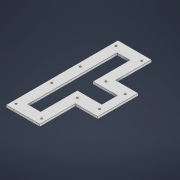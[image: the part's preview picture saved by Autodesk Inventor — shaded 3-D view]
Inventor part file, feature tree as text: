
AUTODESK INVENTOR PART (.ipt)
format: ipt  version: 2021 (Build 250183000, 183)  size: 371,712 bytes
history: native  units: mm
features: extrude x5, sketch x4, projected_geometry x1
ambient origin geometry x8: Origin, YZ Plane, XZ Plane, XY Plane, X Axis, Y Axis, Z Axis, Center Point
bodies: Volumenkörper1 (feature_tree)
feature tree (10):
  extrude  "Extrusion1"  Depth=200.0mm
  extrude  "Extrusion3"  Depth=2.0mm
  extrude  "Extrusion2"  Depth=10.5mm
  extrude  "Extrusion4"  Depth=2.0mm
  extrude  "Extrusion5"  Depth=2.0mm
  sketch  "Skizze1"  dims[d0=60.0mm d1=200.0mm]
  sketch  "Skizze3"  dims[d2=2.0mm d3=0.0mm d4=3.2mm]
  sketch  "Skizze4"  dims[d5=3.2mm d6=10.5mm]
  projected_geometry  "Projizierte Kontur1"
  sketch  "Skizze5"  dims[d7=10.5mm d8=23.0mm d9=23.0mm d10=3.2mm d11=3.2mm d12=23.0mm d13=23.0mm d14=25.5mm d15=25.5mm d16=5.0mm d17=5.0mm d19=4.0mm d20=5.0mm d23=4.0mm d24=4.0mm d25=4.0mm d26=4.0mm d27=4.0mm d28=4.0mm d29=4.0mm d30=4.0mm d31=4.0mm d32=4.0mm d33=4.0mm d34=4.0mm d35=4.0mm d36=4.0mm d37=4.0mm d38=4.0mm d39=4.0mm d40=4.0mm d41=4.0mm d42=4.0mm d43=4.0mm d44=4.0mm d45=4.0mm d48=12.6mm d49=12.6mm d50=12.6mm d51=12.6mm d52=12.6mm d53=12.6mm d54=2.0mm d55=0.0mm d56=40.0mm d57=0.0mm d58=3.2mm d59=3.2mm d60=23.0mm d61=23.0mm d64=37.0mm d65=37.0mm d66=4.0mm d67=4.0mm d68=4.0mm d69=4.0mm d70=4.0mm d71=4.0mm d72=4.0mm d73=4.0mm d74=4.0mm d75=4.0mm d76=4.0mm d77=15.6mm d78=15.6mm d79=2.0mm d80=0.0mm d81=10.0mm d82=10.0mm d83=8.0mm d84=8.0mm d85=15.0mm d86=10.0mm d87=10.0mm d88=18.6mm d89=18.6mm d90=2.0mm d91=0.0mm]
